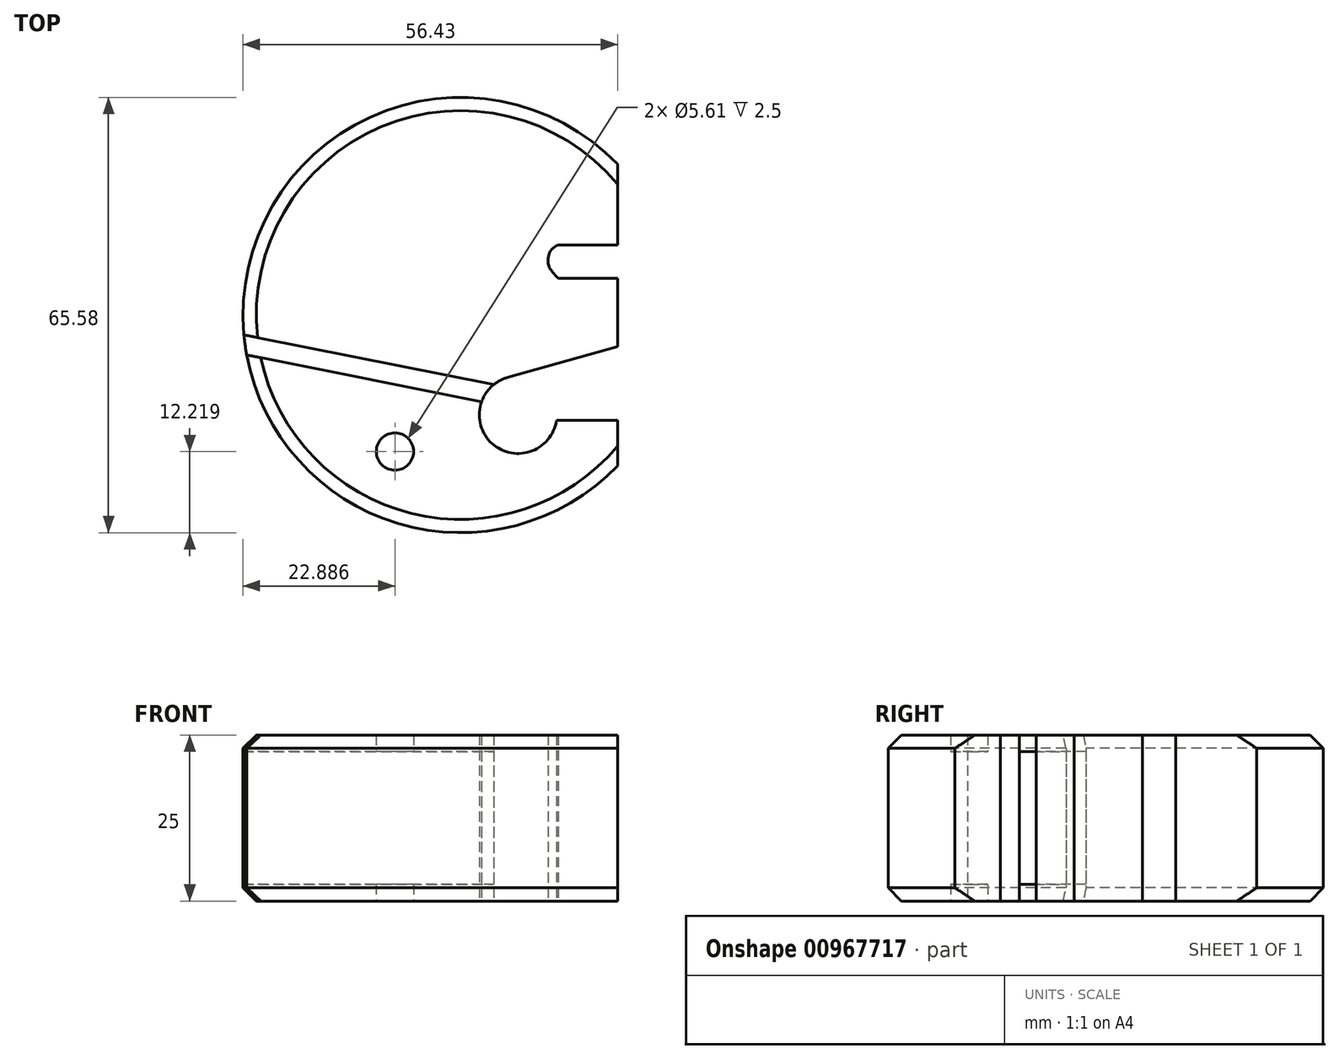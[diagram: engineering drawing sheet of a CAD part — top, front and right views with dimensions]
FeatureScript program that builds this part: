
annotation { "Feature Type Name" : "Feature", "Feature Type Description" : "" }
export const myFeature = defineFeature(function(context is Context, id is Id, definition is map)
    precondition{}
    {
        {
            var Q0;
            Q0=qCreatedBy(makeId("Top.planeOp"),FACE);
            var sketch = newSketch(context, id + "F0", { "sketchPlane" : qUnion([Q0])});
            skCircle(sketch, "E0", {"center": v(0, 0) * mm, "radius": 32.79 * mm});
            skLineSegment(sketch, "E1", {"start": v(23.64, -22.72) * mm, "end": v(23.64, -15.88) * mm});
            skLineSegment(sketch, "E2", {"start": v(23.64, -15.88) * mm, "end": v(14.42, -15.88) * mm});
            skCircle(sketch, "E3", {"center": v(8.65, -15.02) * mm, "radius": 5.84 * mm});
            skPoint(sketch, "E3.second.point", {"position": v(2.88, -14.1) * mm});
            skPoint(sketch, "E3.third.point", {"position": v(3.15, -13.04) * mm});
            skFitSpline(sketch, "E4", {"points": [v(14.7, 5.54) * mm, v(13.2, 7.8) * mm, v(14.7, 10.56) * mm], "startDerivative": vector(-5.43, 5.75) * mm, "endDerivative": vector(7.85, 2.64) * mm});
            skLineSegment(sketch, "E5", {"start": v(14.7, 10.56) * mm, "end": v(23.64, 10.56) * mm});
            skLineSegment(sketch, "E6", {"start": v(23.64, 10.56) * mm, "end": v(23.64, 22.72) * mm});
            skLineSegment(sketch, "E7", {"start": v(23.64, 5.54) * mm, "end": v(14.7, 5.54) * mm});
            skCircle(sketch, "E8", {"center": v(-9.9, -20.57) * mm, "radius": 2.8 * mm});
            skLineSegment(sketch, "E9", {"start": v(3.15, -13.04) * mm, "end": v(-32.23, -6) * mm});
            skLineSegment(sketch, "E10", {"start": v(-32.65, -2.98) * mm, "end": v(5, -10.47) * mm});
            skLineSegment(sketch, "E11", {"start": v(23.64, 5.54) * mm, "end": v(23.64, -4.75) * mm});
            skLineSegment(sketch, "E12", {"start": v(23.64, -4.75) * mm, "end": v(7.07, -9.4) * mm});
            skSolve(sketch);
        }
        {
            var Q0;
            Q0=makeQuery(id+"F0.imprint","IMPRINT",FACE,{"disambiguationData":[TD([[makeQuery(id+"F0.imprint","IMPRINT",EDGE,{"derivedFrom":sQuery(id+"F0.wireOp",EDGE,"E4")}),1.0]])]});
            var Q1;
            {var subQ3=sQuery(id+"F0.wireOp",EDGE,"E1");Q1=makeQuery(id+"F0.imprint","IMPRINT",FACE,{"disambiguationData":[TD([[makeQuery(id+"F0.imprint","IMPRINT",EDGE,{"derivedFrom":subQ3}),1.0]])]});}
            extrude(context, id + "F1", {"entities" : qUnion([Q0, Q1]), "depth" : 12.5 * mm, "offsetDistance" : 25 * mm, "hasSecondDirection" : true, "secondDirectionOppositeDirection" : true, "secondDirectionDepth" : 12.5 * mm});
        }
        {
            var Q0;
            {var subQ0=sQuery(id+"F0.wireOp",EDGE,"E9");Q0=makeQuery(id+"F0.imprint","IMPRINT",FACE,{"disambiguationData":[TD([[makeQuery(id+"F0.imprint","IMPRINT",EDGE,{"derivedFrom":subQ0}),-1.0]])]});}
            extrude(context, id + "F2", {"entities" : qUnion([Q0]), "depth" : 10 * mm, "offsetDistance" : 25 * mm, "hasSecondDirection" : true, "secondDirectionOppositeDirection" : true, "secondDirectionDepth" : 10 * mm});
        }
        {
            var Q0;
            Q0=makeQuery(id+"F0.imprint","IMPRINT",FACE,{"disambiguationData":[TD([[makeQuery(id+"F0.imprint","IMPRINT",EDGE,{"derivedFrom":sQuery(id+"F0.wireOp",EDGE,"E8")}),1.0]])]});
            extrude(context, id + "F3", {"entities" : qUnion([Q0]), "operationType" : NewBodyOperationType.ADD, "depth" : 10 * mm, "offsetDistance" : 25 * mm, "hasSecondDirection" : true, "secondDirectionOppositeDirection" : true, "secondDirectionDepth" : 10 * mm});
        }
        {
            var Q0;
            {var subQ0=sQuery(id+"F0.wireOp",EDGE,"E0");Q0=makeQuery(id+"F1.opExtrude","CAP_EDGE",EDGE,{"disambiguationData":[OSD([subQ0]),TDD([makeQuery(id+"F0.imprint","IMPRINT",EDGE,{"disambiguationData":[TD([[makeQuery(id+"F0.imprint","INTERSECT",VERTEX,{"derivedFrom":[subQ0,sQuery(id+"F0.wireOp",EDGE,"E6")]}),-1.0]])],"derivedFrom":subQ0})])],"isStart":false});}
            var Q1;
            {var subQ0=sQuery(id+"F0.wireOp",EDGE,"E0");Q1=makeQuery(id+"F1.opExtrude","CAP_EDGE",EDGE,{"disambiguationData":[OSD([subQ0]),TDD([makeQuery(id+"F0.imprint","IMPRINT",EDGE,{"disambiguationData":[TD([[makeQuery(id+"F0.imprint","INTERSECT",VERTEX,{"derivedFrom":[subQ0,sQuery(id+"F0.wireOp",EDGE,"E1")]}),1.0]])],"derivedFrom":subQ0})])],"isStart":false});}
            var Q2;
            {var subQ0=sQuery(id+"F0.wireOp",EDGE,"E0");Q2=makeQuery(id+"F1.opExtrude","CAP_EDGE",EDGE,{"disambiguationData":[OSD([subQ0]),TDD([makeQuery(id+"F0.imprint","IMPRINT",EDGE,{"disambiguationData":[TD([[makeQuery(id+"F0.imprint","INTERSECT",VERTEX,{"derivedFrom":[subQ0,sQuery(id+"F0.wireOp",EDGE,"E6")]}),-1.0]])],"derivedFrom":subQ0})])],"isStart":true});}
            var Q3;
            {var subQ0=sQuery(id+"F0.wireOp",EDGE,"E0");Q3=makeQuery(id+"F1.opExtrude","CAP_EDGE",EDGE,{"disambiguationData":[OSD([subQ0]),TDD([makeQuery(id+"F0.imprint","IMPRINT",EDGE,{"disambiguationData":[TD([[makeQuery(id+"F0.imprint","INTERSECT",VERTEX,{"derivedFrom":[subQ0,sQuery(id+"F0.wireOp",EDGE,"E1")]}),1.0]])],"derivedFrom":subQ0})])],"isStart":true});}
            chamfer(context, id + "F4", {"entities" : qUnion([Q0, Q1, Q2, Q3]), "width" : 2 * mm, "tangentPropagation" : true});
        }
    });
